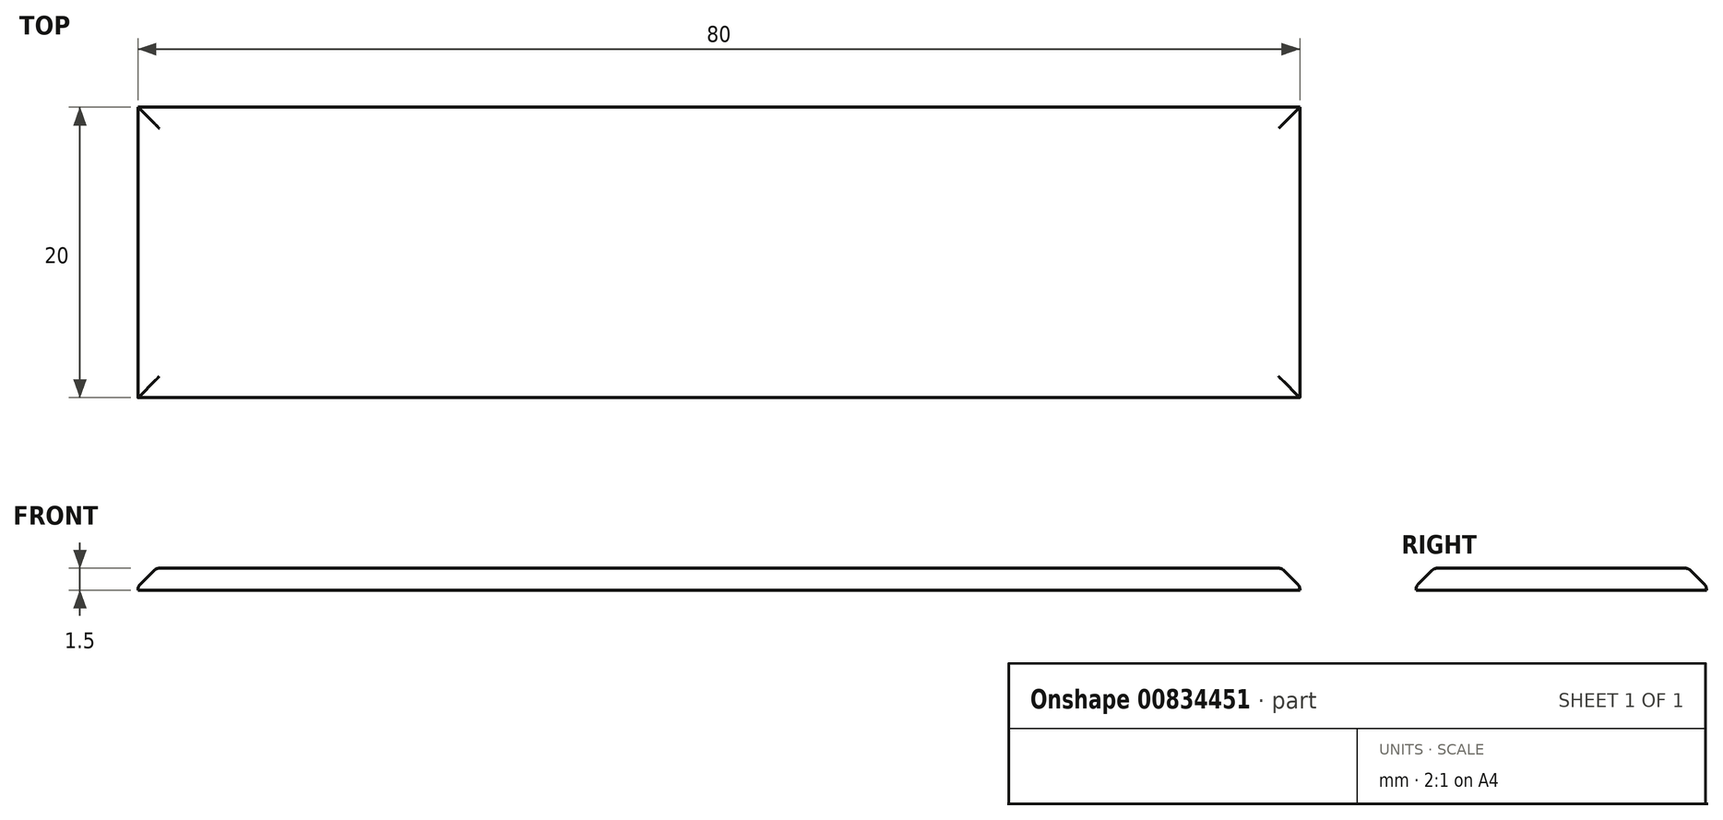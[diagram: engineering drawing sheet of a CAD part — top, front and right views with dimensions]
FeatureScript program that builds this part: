
annotation { "Feature Type Name" : "Feature", "Feature Type Description" : "" }
export const myFeature = defineFeature(function(context is Context, id is Id, definition is map)
    precondition{}
    {
        {
            var Q0;
            Q0=qCreatedBy(makeId("Top.planeOp"),FACE);
            var sketch = newSketch(context, id + "F0", { "sketchPlane" : qUnion([Q0])});
            skLineSegment(sketch, "E0.bottom", {"start": v(0, 0) * mm, "end": v(80, 0) * mm});
            skLineSegment(sketch, "E0.top", {"start": v(0, 20) * mm, "end": v(80, 20) * mm});
            skLineSegment(sketch, "E0.left", {"start": v(0, 0) * mm, "end": v(0, 20) * mm});
            skLineSegment(sketch, "E0.right", {"start": v(80, 0) * mm, "end": v(80, 20) * mm});
            skSolve(sketch);
        }
        {
            var Q0;
            Q0=makeQuery(id+"F0.imprint","IMPRINT",FACE,{"disambiguationData":[TD([[makeQuery(id+"F0.imprint","IMPRINT",EDGE,{"derivedFrom":sQuery(id+"F0.wireOp",EDGE,"E0.bottom")}),1.0]])]});
            extrude(context, id + "F1", {"entities" : qUnion([Q0]), "depth" : 1.5 * mm, "offsetDistance" : 25 * mm});
        }
        {
            var Q0;
            Q0=makeQuery(id+"F1.opExtrude","CAP_FACE",FACE,{"disambiguationData":[OSD([sQuery(id+"F0.wireOp",EDGE,"E0.bottom"),sQuery(id+"F0.wireOp",EDGE,"E0.top"),sQuery(id+"F0.wireOp",EDGE,"E0.left"),sQuery(id+"F0.wireOp",EDGE,"E0.right")])],"isStart":false});
            chamfer(context, id + "F2", {"entities" : qUnion([Q0]), "width" : 1.25 * mm, "tangentPropagation" : true});
        }
        {
            var Q0;
            Q0=makeQuery(id+"F1.opExtrude","CAP_FACE",FACE,{"disambiguationData":[OSD([sQuery(id+"F0.wireOp",EDGE,"E0.bottom"),sQuery(id+"F0.wireOp",EDGE,"E0.top"),sQuery(id+"F0.wireOp",EDGE,"E0.left"),sQuery(id+"F0.wireOp",EDGE,"E0.right")])],"isStart":false});
            var Q1;
            {var subQ0=sQuery(id+"F0.wireOp",EDGE,"E0.right");Q1=makeQuery(id+"F2.opChamfer","BLEND_EDGE",EDGE,{"blendedFrom":[makeQuery(id+"F1.opExtrude","CAP_EDGE",EDGE,{"disambiguationData":[OSD([subQ0])],"isStart":false}),makeQuery(id+"F1.opExtrude","SWEPT_FACE",FACE,{"disambiguationData":[OSD([subQ0])]})],"blendedInto":[makeQuery(id+"F1.opExtrude","SWEPT_FACE",FACE,{"disambiguationData":[OSD([subQ0])]})]});}
            var Q2;
            {var subQ0=sQuery(id+"F0.wireOp",EDGE,"E0.bottom");Q2=makeQuery(id+"F2.opChamfer","BLEND_EDGE",EDGE,{"blendedFrom":[makeQuery(id+"F1.opExtrude","CAP_EDGE",EDGE,{"disambiguationData":[OSD([subQ0])],"isStart":false}),makeQuery(id+"F1.opExtrude","SWEPT_FACE",FACE,{"disambiguationData":[OSD([subQ0])]})],"blendedInto":[makeQuery(id+"F1.opExtrude","SWEPT_FACE",FACE,{"disambiguationData":[OSD([subQ0])]})]});}
            var Q3;
            {var subQ0=sQuery(id+"F0.wireOp",EDGE,"E0.top");Q3=makeQuery(id+"F2.opChamfer","BLEND_EDGE",EDGE,{"blendedFrom":[makeQuery(id+"F1.opExtrude","CAP_EDGE",EDGE,{"disambiguationData":[OSD([subQ0])],"isStart":false}),makeQuery(id+"F1.opExtrude","SWEPT_FACE",FACE,{"disambiguationData":[OSD([subQ0])]})],"blendedInto":[makeQuery(id+"F1.opExtrude","SWEPT_FACE",FACE,{"disambiguationData":[OSD([subQ0])]})]});}
            var Q4;
            {var subQ0=sQuery(id+"F0.wireOp",EDGE,"E0.left");Q4=makeQuery(id+"F2.opChamfer","BLEND_EDGE",EDGE,{"blendedFrom":[makeQuery(id+"F1.opExtrude","CAP_EDGE",EDGE,{"disambiguationData":[OSD([subQ0])],"isStart":false}),makeQuery(id+"F1.opExtrude","SWEPT_FACE",FACE,{"disambiguationData":[OSD([subQ0])]})],"blendedInto":[makeQuery(id+"F1.opExtrude","SWEPT_FACE",FACE,{"disambiguationData":[OSD([subQ0])]})]});}
            fillet(context, id + "F3", {"entities" : qUnion([Q0, Q1, Q2, Q3, Q4]), "radius" : .50 * mm, "tangentPropagation" : true, "allowEdgeOverflow" : false});
        }
    });
